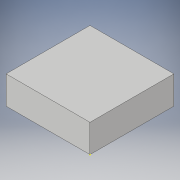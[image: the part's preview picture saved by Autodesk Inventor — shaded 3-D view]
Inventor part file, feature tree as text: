
AUTODESK INVENTOR PART (.ipt)
format: ipt  version: 2019.4 (Build 234330000, 330)  size: 87,040 bytes
history: native  units: in
note: dims shown in document units (in); Inventor stores cm internally (conversion verified against a paired STEP export)
features: sketch x2, extrude x1
ambient origin geometry x8: Origin, YZ Plane, XZ Plane, XY Plane, X Axis, Y Axis, Z Axis, Center Point
bodies: Solid1 (feature_tree)
feature tree (3):
  sketch  "Sketch1"  dims[d0=1.1811in d1=1.1811in]
  extrude  "Extrusion1"  Depth=1.1811in
  sketch  "Sketch2"  dims[d2=0.3937in d3=0.0in]
